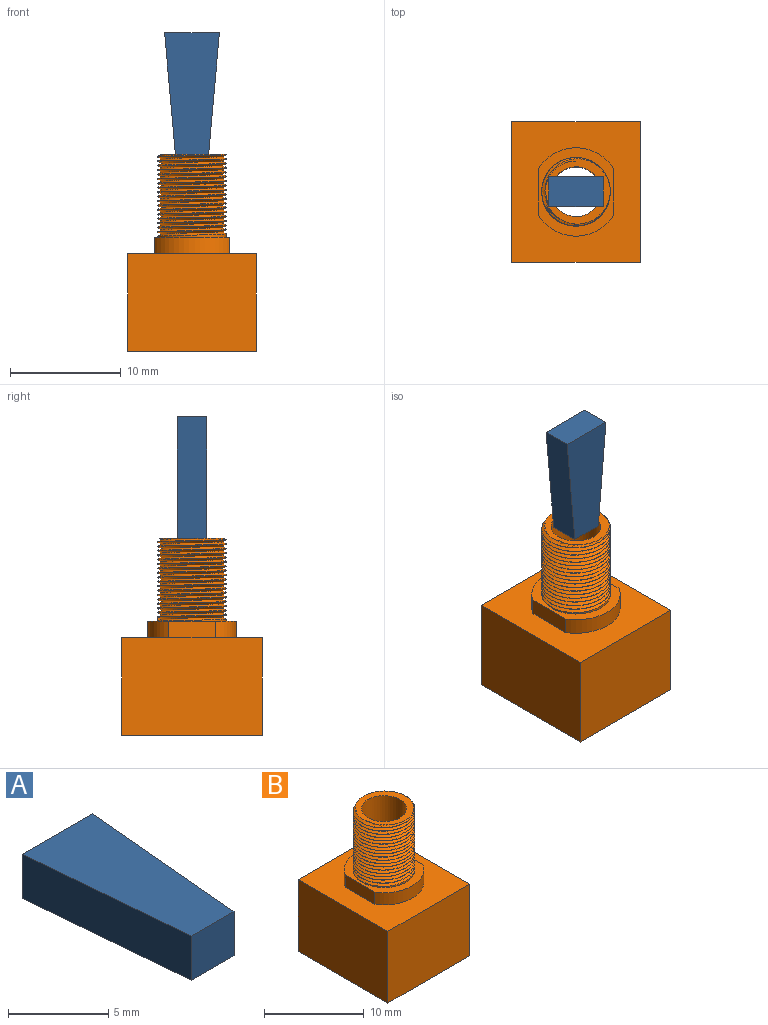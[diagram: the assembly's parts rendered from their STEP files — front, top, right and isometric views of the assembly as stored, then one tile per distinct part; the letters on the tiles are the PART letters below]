
ASSEMBLY  parts=2 mates=1
PART A: 6 faces, bbox 5x11x2.7 mm
  f0: plane 11x2.7mm, normal (-1,-0.09,0), area 29.8mm2, adj f1,f3,f4,f5
  f1: plane 3x2.7mm, normal (0,-1,0), area 8.1mm2, adj f0,f2,f4,f5
  f2: plane 11x2.7mm, normal (1,-0.09,0), area 29.8mm2, adj f1,f3,f4,f5
  f3: plane 4.96x2.7mm, normal (0,1,0), area 13.4mm2, adj f0,f2,f4,f5
  f4: plane 11x4.96mm, normal (0,0,1), area 43.8mm2, adj f0,f1,f2,f3
  f5: plane 11x4.96mm, normal (0,0,-1), area 43.8mm2, adj f0,f1,f2,f3
PART B: 17 faces, bbox 11.9x13x18.3 mm
  f0: plane 11.6x8.8mm, normal (0,1,0), area 102.1mm2, adj f1,f3,f4,f5
  f1: plane 12.7x8.8mm, normal (-1,0,0), area 111.8mm2, adj f0,f2,f4,f5
  f2: plane 11.6x8.8mm, normal (0,-1,0), area 102.1mm2, adj f1,f3,f4,f5
  f3: plane 12.7x8.8mm, normal (1,0,0), area 111.8mm2, adj f0,f2,f4,f5
  f4: plane 12.7x11.6mm, normal (0,0,1), area 100.5mm2, adj f0,f1,f2,f3,f6,f7,f8,f9
  f5: plane 12.7x11.6mm, normal (0,0,-1), area 131.4mm2, adj f0,f1,f2,f3,f16
  f6: cylinder r=4mm len=6.8mm, axis (0,0,-1), area 12.2mm2, adj f4,f7,f9,f10
  f7: plane 4.21x1.5mm, normal (-1,0,0), area 6.3mm2, adj f4,f6,f8,f10
  f8: cylinder r=4mm len=6.8mm, axis (0,0,-1), area 12.2mm2, adj f4,f7,f9,f10
  f9: plane 4.21x1.5mm, normal (1,0,0), area 6.3mm2, adj f4,f6,f8,f10
  f10: plane 8x6.8mm, normal (0,0,1), area 16.6mm2, adj f6,f7,f8,f9,f11
  f11: cylinder r=3.1mm len=7.5mm, axis (0,0,-1), area 15.8mm2, adj f10,f12,f13,f14,f15
  f12: plane 6.19x6.19mm, normal (0,0,1), area 11.5mm2, adj f11,f14,f15,f16
  f13: plane 0.37x0.32mm, normal (-1,0,0), area 0.1mm2, adj f11,f14,f15
  f14: bspline ~7.72x7.16mm, area 126.8mm2, adj f11,f12,f13,f15
  f15: bspline ~7.59x7.16mm, area 123.5mm2, adj f11,f12,f13,f14
  f16: cylinder r=2.25mm len=17.8mm, axis (0,0,1), area 251.6mm2, adj f5,f12
PLACE A rot(axis=(1,0,0),90deg) t=(-5.49,5.21,19.32)mm
PLACE B t=(-5.49,3.86,1.52)mm
MATE fastened A.f1 <-> B.f11  axis (0,0,-1) through (-5.49,3.86,19.32)mm
